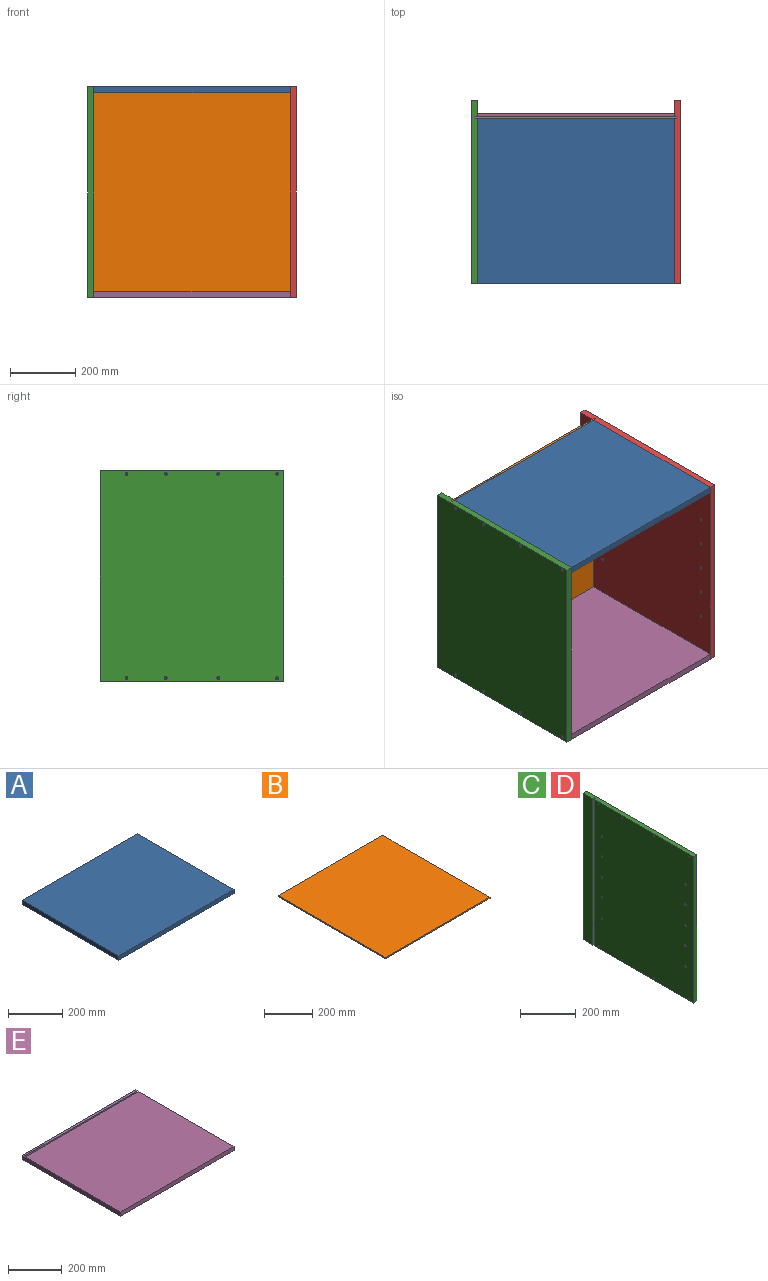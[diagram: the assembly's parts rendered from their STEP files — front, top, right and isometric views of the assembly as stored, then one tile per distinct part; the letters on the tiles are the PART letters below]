
ASSEMBLY  parts=5 mates=12
PART A: 6 faces, bbox 600x504x19 mm
  f0: plane 504x19mm, normal (-1,0,0), area 9576mm2, adj f1,f3,f4,f5
  f1: plane 600x19mm, normal (0,-1,0), area 11400mm2, adj f0,f2,f4,f5
  f2: plane 504x19mm, normal (1,0,0), area 9576mm2, adj f1,f3,f4,f5
  f3: plane 600x19mm, normal (0,1,0), area 11400mm2, adj f0,f2,f4,f5
  f4: plane 600x504mm, normal (0,0,1), area 302400mm2, adj f0,f1,f2,f3
  f5: plane 600x504mm, normal (0,0,-1), area 302400mm2, adj f0,f1,f2,f3
PART B: 6 faces, bbox 616x632x6 mm
  f0: plane 632x6mm, normal (-1,0,0), area 3792mm2, adj f1,f3,f4,f5
  f1: plane 616x6mm, normal (0,-1,0), area 3696mm2, adj f0,f2,f4,f5
  f2: plane 632x6mm, normal (1,0,0), area 3792mm2, adj f1,f3,f4,f5
  f3: plane 616x6mm, normal (0,1,0), area 3696mm2, adj f0,f2,f4,f5
  f4: plane 632x616mm, normal (0,0,1), area 389312mm2, adj f0,f1,f2,f3
  f5: plane 632x616mm, normal (0,0,-1), area 389312mm2, adj f0,f1,f2,f3
PART C: 46 faces, bbox 19x560x643 mm
  f0: plane 643x50mm, normal (-1,0,0), area 32150mm2, adj f1,f3,f4,f23
  f1: plane 560x19mm, normal (0,0,1), area 10592mm2, adj f0,f2,f4,f5,f6,f23,f24,f25
  f2: plane 643x19mm, normal (0,-1,0), area 12217mm2, adj f1,f3,f5,f6
  f3: plane 560x19mm, normal (0,0,-1), area 10592mm2, adj f0,f2,f4,f5,f6,f23,f24,f25
  f4: plane 643x19mm, normal (0,1,0), area 12217mm2, adj f0,f1,f3,f5
  f5: plane 643x560mm, normal (1,0,0), area 359575.6mm2, adj f1,f2,f3,f4,f8,f10,f12,f14
  f6: plane 643x504mm, normal (-1,0,0), area 323442.1mm2, adj f1,f2,f3,f7,f9,f11,f13,f15
  f7: cylinder r=2.25mm len=16.77mm, axis (1,0,0), area 237.1mm2, adj f6,f8
  f8: cone r=2.25mm half-angle=45deg, axis (1,0,0), area 66.7mm2, adj f5,f7
  f9: cylinder r=2.25mm len=16.77mm, axis (1,0,0), area 237.1mm2, adj f6,f10
  f10: cone r=2.25mm half-angle=45deg, axis (1,0,0), area 66.7mm2, adj f5,f9
  f11: cylinder r=2.25mm len=16.77mm, axis (1,0,0), area 237.1mm2, adj f6,f12
  f12: cone r=2.25mm half-angle=45deg, axis (1,0,0), area 66.7mm2, adj f5,f11
  f13: cylinder r=2.25mm len=16.77mm, axis (1,0,0), area 237.1mm2, adj f6,f14
  f14: cone r=2.25mm half-angle=45deg, axis (1,0,0), area 66.7mm2, adj f5,f13
  f15: cylinder r=2.25mm len=16.77mm, axis (1,0,0), area 237.1mm2, adj f6,f16
  f16: cone r=2.25mm half-angle=45deg, axis (1,0,0), area 66.7mm2, adj f5,f15
  f17: cylinder r=2.25mm len=16.77mm, axis (1,0,0), area 237.1mm2, adj f6,f18
  f18: cone r=2.25mm half-angle=45deg, axis (1,0,0), area 66.7mm2, adj f5,f17
  f19: cylinder r=2.25mm len=16.77mm, axis (1,0,0), area 237.1mm2, adj f6,f20
  f20: cone r=2.25mm half-angle=45deg, axis (1,0,0), area 66.7mm2, adj f5,f19
  f21: cylinder r=2.25mm len=16.77mm, axis (1,0,0), area 237.1mm2, adj f6,f22
  f22: cone r=2.25mm half-angle=45deg, axis (1,0,0), area 66.7mm2, adj f5,f21
  f23: plane 643x8mm, normal (0,-1,0), area 5144mm2, adj f0,f1,f3,f25
  f24: plane 643x8mm, normal (0,1,0), area 5144mm2, adj f1,f3,f6,f25
  f25: plane 643x6mm, normal (-1,0,0), area 3858mm2, adj f1,f3,f23,f24
  f26: cone r=0mm half-angle=59deg, axis (-1,0,0), area 58.6mm2, adj f27
  f27: cylinder r=4mm len=12mm, axis (-1,0,0), area 301.6mm2, adj f6,f26
  f28: cone r=0mm half-angle=59deg, axis (-1,0,0), area 58.6mm2, adj f29
  f29: cylinder r=4mm len=12mm, axis (-1,0,0), area 301.6mm2, adj f6,f28
  f30: cone r=0mm half-angle=59deg, axis (-1,0,0), area 58.6mm2, adj f31
  f31: cylinder r=4mm len=12mm, axis (-1,0,0), area 301.6mm2, adj f6,f30
  f32: cone r=0mm half-angle=59deg, axis (-1,0,0), area 58.6mm2, adj f33
  f33: cylinder r=4mm len=12mm, axis (-1,0,0), area 301.6mm2, adj f6,f32
  f34: cone r=0mm half-angle=59deg, axis (-1,0,0), area 58.6mm2, adj f35
  f35: cylinder r=4mm len=12mm, axis (-1,0,0), area 301.6mm2, adj f6,f34
  f36: cone r=0mm half-angle=59deg, axis (-1,0,0), area 58.6mm2, adj f37
  f37: cylinder r=4mm len=12mm, axis (-1,0,0), area 301.6mm2, adj f6,f36
  f38: cone r=0mm half-angle=59deg, axis (-1,0,0), area 58.6mm2, adj f39
  f39: cylinder r=4mm len=12mm, axis (-1,0,0), area 301.6mm2, adj f6,f38
  f40: cone r=0mm half-angle=59deg, axis (-1,0,0), area 58.6mm2, adj f41
  f41: cylinder r=4mm len=12mm, axis (-1,0,0), area 301.6mm2, adj f6,f40
  f42: cone r=0mm half-angle=59deg, axis (-1,0,0), area 58.6mm2, adj f43
  f43: cylinder r=4mm len=12mm, axis (-1,0,0), area 301.6mm2, adj f6,f42
  f44: cone r=0mm half-angle=59deg, axis (-1,0,0), area 58.6mm2, adj f45
  f45: cylinder r=4mm len=12mm, axis (-1,0,0), area 301.6mm2, adj f6,f44
PART D: same geometry as C
PART E: 18 faces, bbox 600x520x19 mm
  f0: plane 600x520mm, normal (0,0,-1), area 308151.5mm2, adj f2,f3,f4,f5,f10,f12,f14,f16
  f1: plane 600x10mm, normal (0,0,1), area 6000mm2, adj f2,f4,f5,f7
  f2: plane 520x19mm, normal (-1,0,0), area 9832mm2, adj f0,f1,f3,f5,f6,f7,f8,f9
  f3: plane 600x19mm, normal (0,-1,0), area 11400mm2, adj f0,f2,f4,f6
  f4: plane 520x19mm, normal (1,0,0), area 9832mm2, adj f0,f1,f3,f5,f6,f7,f8,f9
  f5: plane 600x19mm, normal (0,1,0), area 11400mm2, adj f0,f1,f2,f4
  f6: plane 600x504mm, normal (0,0,1), area 302400mm2, adj f2,f3,f4,f8
  f7: plane 600x8mm, normal (0,-1,0), area 4800mm2, adj f1,f2,f4,f9
  f8: plane 600x8mm, normal (0,1,0), area 4800mm2, adj f2,f4,f6,f9
  f9: plane 600x6mm, normal (0,0,1), area 3600mm2, adj f2,f4,f7,f8
  f10: cylinder r=17.5mm len=35mm, axis (0,0,-1), area 1099.6mm2, adj f0,f11
  f11: plane 35x35mm, normal (0,0,-1), area 962.1mm2, adj f10
  f12: cylinder r=17.5mm len=35mm, axis (0,0,-1), area 1099.6mm2, adj f0,f13
  f13: plane 35x35mm, normal (0,0,-1), area 962.1mm2, adj f12
  f14: cylinder r=17.5mm len=35mm, axis (0,0,-1), area 1099.6mm2, adj f0,f15
  f15: plane 35x35mm, normal (0,0,-1), area 962.1mm2, adj f14
  f16: cylinder r=17.5mm len=35mm, axis (0,0,-1), area 1099.6mm2, adj f0,f17
  f17: plane 35x35mm, normal (0,0,-1), area 962.1mm2, adj f16
PLACE A rot(axis=(0,1,0),0deg) t=(-619,0,302.5)mm
PLACE B rot(axis=(1,0,0),90deg) t=(-627,510,-310.5)mm
PLACE C rot(axis=(0,1,0),180deg) t=(-619,0,321.5)mm
PLACE D t=(-19,0,-321.5)mm
PLACE E rot(axis=(0,1,0),0deg) t=(-619,0,-321.5)mm
MATE planar C.f3 <-> D.f1  axis (0,0,1) through (-628.52,278.97,321.5)mm
MATE planar E.f3 <-> D.f2  axis (0,-1,0) through (-319,0,-312)mm
MATE planar A.f1 <-> C.f2  axis (0,-1,0) through (-319,0,312)mm
MATE planar B.f4 <-> A.f3  axis (0,-1,0) through (-319,504,5.5)mm
MATE planar E.f0 <-> C.f1  axis (0,0,-1) through (-19,0,-321.5)mm
MATE planar E.f2 <-> C.f6  axis (-1,0,0) through (-619,258.79,-312.03)mm
MATE planar A.f2 <-> D.f6  axis (1,0,0) through (-19,252,312)mm
MATE planar B.f1 <-> E.f9  axis (0,0,-1) through (-319,507,-310.5)mm
MATE planar E.f3 <-> C.f2  axis (0,-1,0) through (-319,0,-312)mm
MATE planar A.f4 <-> C.f3  axis (0,0,1) through (-619,252,321.5)mm
MATE planar E.f4 <-> D.f6  axis (1,0,0) through (-19,258.79,-312.03)mm
MATE planar B.f2 <-> D.f25  axis (1,0,0) through (-11,507,5.5)mm
